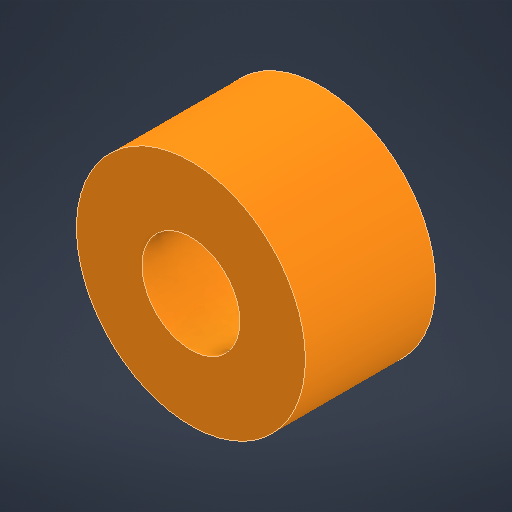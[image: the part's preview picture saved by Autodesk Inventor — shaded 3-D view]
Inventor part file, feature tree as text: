
AUTODESK INVENTOR PART (.ipt)
format: ipt  version: 2025.3 (Build 293356030, 356C)  size: 171,008 bytes
history: native  units: mm
features: other x1, extrude x1, sketch x1
ambient origin geometry x8: Origin, YZ Plane, XZ Plane, XY Plane, X Axis, Y Axis, Z Axis, Center Point
bodies: Body1 (feature_tree)
feature tree (3):
  other  "實體1"
  extrude  "擠出1"  Depth=2.0mm
  sketch  "草圖1"
